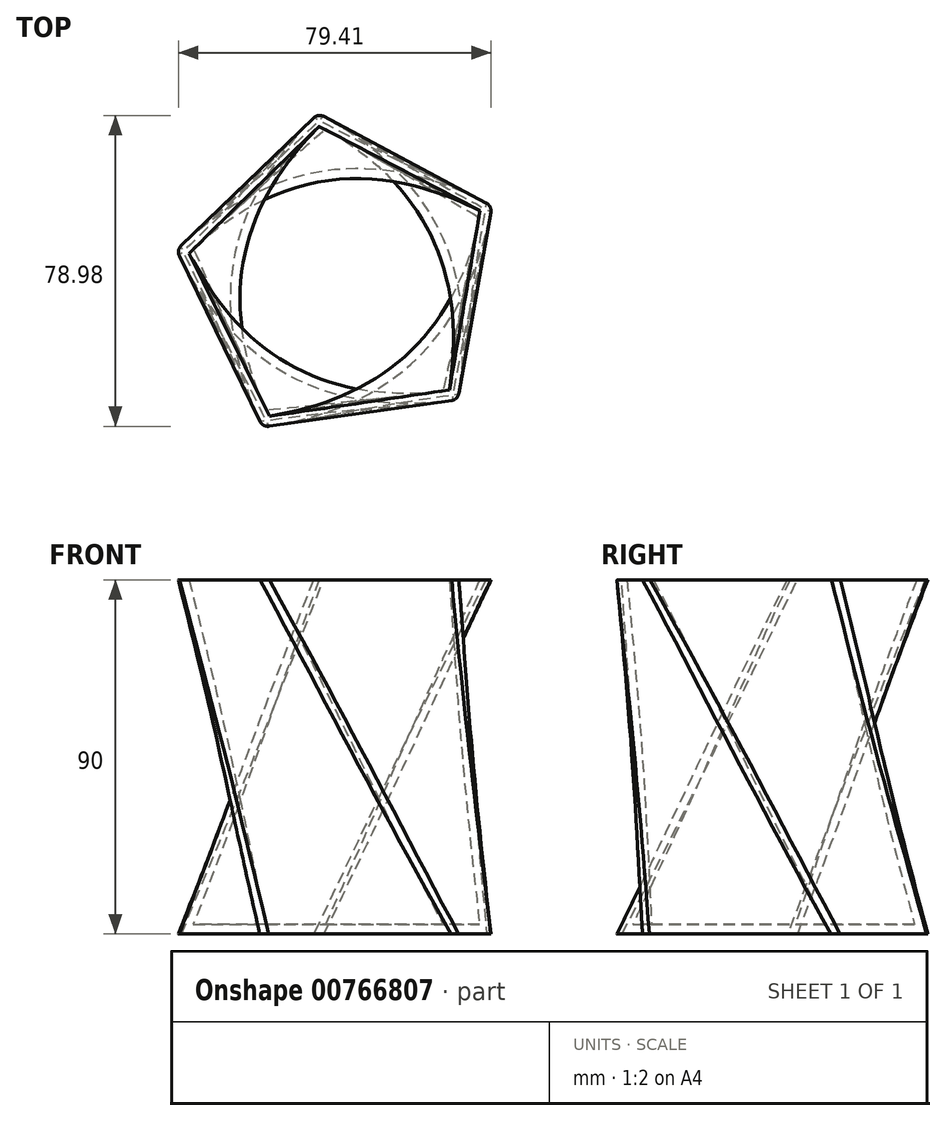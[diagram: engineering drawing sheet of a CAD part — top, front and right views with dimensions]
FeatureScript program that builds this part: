
annotation { "Feature Type Name" : "Feature", "Feature Type Description" : "" }
export const myFeature = defineFeature(function(context is Context, id is Id, definition is map)
    precondition{}
    {
        {
            var Q0;
            Q0=qCreatedBy(makeId("Top.planeOp"),FACE);
            var sketch = newSketch(context, id + "F0", { "sketchPlane" : qUnion([Q0])});
            skCircle(sketch, "E0.cCircle", {"center": v(0, 0) * mm, "radius": 34.4 * mm, "construction": true});
            skLineSegment(sketch, "E0.0", {"start": v(-5.9, 42.12) * mm, "end": v(38.24, 18.63) * mm});
            skLineSegment(sketch, "E0.1", {"start": v(38.24, 18.63) * mm, "end": v(29.53, -30.6) * mm});
            skLineSegment(sketch, "E0.2", {"start": v(29.53, -30.6) * mm, "end": v(-19.98, -37.55) * mm});
            skLineSegment(sketch, "E0.3", {"start": v(-19.98, -37.55) * mm, "end": v(-41.88, 7.4) * mm});
            skLineSegment(sketch, "E0.4", {"start": v(-41.88, 7.4) * mm, "end": v(-5.9, 42.12) * mm});
            skPoint(sketch, "E0.0.midPoint", {"position": v(16.17, 30.37) * mm});
            skSolve(sketch);
        }
        {
            var Q0;
            Q0=qCreatedBy(makeId("Top.planeOp"),FACE);
            cPlane(context, id + "F1", {"entities" : qUnion([Q0]), "cplaneType" : CPlaneType.OFFSET, "offset" : 90 * mm, "width" : 150 * mm, "height" : 150 * mm});
        }
        {
            var Q0;
            Q0=qCreatedBy(id+"F1.planeOp",FACE);
            var sketch = newSketch(context, id + "F2", { "sketchPlane" : qUnion([Q0])});
            skLineSegment(sketch, "E1.0.0", {"start": v(-5.9, 42.12) * mm, "end": v(-41.88, 7.4) * mm});
            skLineSegment(sketch, "E1.0.1", {"start": v(-41.88, 7.4) * mm, "end": v(-19.98, -37.55) * mm});
            skLineSegment(sketch, "E1.0.2", {"start": v(-19.98, -37.55) * mm, "end": v(29.53, -30.6) * mm});
            skLineSegment(sketch, "E1.0.3", {"start": v(29.53, -30.6) * mm, "end": v(38.24, 18.63) * mm});
            skLineSegment(sketch, "E1.0.4", {"start": v(38.24, 18.63) * mm, "end": v(-5.9, 42.12) * mm});
            skSolve(sketch);
        }
        {
            var Q0;
            Q0=makeQuery(id+"F2.imprint","IMPRINT",FACE,{"disambiguationData":[TD([[makeQuery(id+"F2.imprint","IMPRINT",EDGE,{"derivedFrom":sQuery(id+"F2.wireOp",EDGE,"E1.0.0")}),1.0]])]});
            var Q1;
            Q1=makeQuery(id+"F0.imprint","IMPRINT",FACE,{"disambiguationData":[TD([[makeQuery(id+"F0.imprint","IMPRINT",EDGE,{"derivedFrom":sQuery(id+"F0.wireOp",EDGE,"E0.0")}),-1.0]])]});
            var Q2;
            Q2=sQuery(id+"F2.wireOp",VERTEX,"E1.0.1.start");
            var Q3;
            Q3=sQuery(id+"F0.wireOp",VERTEX,"E0.3.start");
            loft(context, id + "F3", {"sheetProfilesArray" : [{ "sheetProfileEntities" : qUnion([Q0]) }, { "sheetProfileEntities" : qUnion([Q1]) }], "matchConnections" : true, "connections" : [{ "connectionEntities" : qUnion([Q2, Q3]), "connectionEdgeQueries" : qUnion([]), "connectionEdgeParameters" : [] }]});
        }
        {
            var Q0;
            Q0=makeQuery(id+"F3.opLoft","CAP_FACE",FACE,{"disambiguationData":[OSD([makeQuery(id+"F2.imprint","IMPRINT",FACE,{"disambiguationData":[TD([[makeQuery(id+"F2.imprint","IMPRINT",EDGE,{"derivedFrom":sQuery(id+"F2.wireOp",EDGE,"E1.0.0")}),1.0]])]})])],"isStart":true});
            shell(context, id + "F4", {"entities" : qUnion([Q0]), "thickness" : 2.5 * mm});
        }
        {
            var Q0;
            Q0=makeQuery(id+"F3.opLoft","SWEPT_EDGE",EDGE,{"disambiguationData":[OSD([sQuery(id+"F0.wireOp",EDGE,"E0.2"),sQuery(id+"F0.wireOp",EDGE,"E0.3"),sQuery(id+"F2.wireOp",EDGE,"E1.0.0"),sQuery(id+"F2.wireOp",EDGE,"E1.0.1")])]});
            var Q1;
            Q1=makeQuery(id+"F3.opLoft","SWEPT_EDGE",EDGE,{"disambiguationData":[OSD([sQuery(id+"F0.wireOp",EDGE,"E0.3"),sQuery(id+"F0.wireOp",EDGE,"E0.4"),sQuery(id+"F2.wireOp",EDGE,"E1.0.0"),sQuery(id+"F2.wireOp",EDGE,"E1.0.4")])]});
            var Q2;
            Q2=makeQuery(id+"F3.opLoft","SWEPT_EDGE",EDGE,{"disambiguationData":[OSD([sQuery(id+"F0.wireOp",EDGE,"E0.0"),sQuery(id+"F0.wireOp",EDGE,"E0.4"),sQuery(id+"F2.wireOp",EDGE,"E1.0.3"),sQuery(id+"F2.wireOp",EDGE,"E1.0.4")])]});
            var Q3;
            Q3=makeQuery(id+"F3.opLoft","SWEPT_EDGE",EDGE,{"disambiguationData":[OSD([sQuery(id+"F0.wireOp",EDGE,"E0.0"),sQuery(id+"F0.wireOp",EDGE,"E0.1"),sQuery(id+"F2.wireOp",EDGE,"E1.0.2"),sQuery(id+"F2.wireOp",EDGE,"E1.0.3")])]});
            var Q4;
            Q4=makeQuery(id+"F3.opLoft","SWEPT_EDGE",EDGE,{"disambiguationData":[OSD([sQuery(id+"F0.wireOp",EDGE,"E0.1"),sQuery(id+"F0.wireOp",EDGE,"E0.2"),sQuery(id+"F2.wireOp",EDGE,"E1.0.1"),sQuery(id+"F2.wireOp",EDGE,"E1.0.2")])]});
            fillet(context, id + "F5", {"entities" : qUnion([Q0, Q1, Q2, Q3, Q4]), "radius" : 2 * mm, "tangentPropagation" : true, "allowEdgeOverflow" : false});
        }
    });
